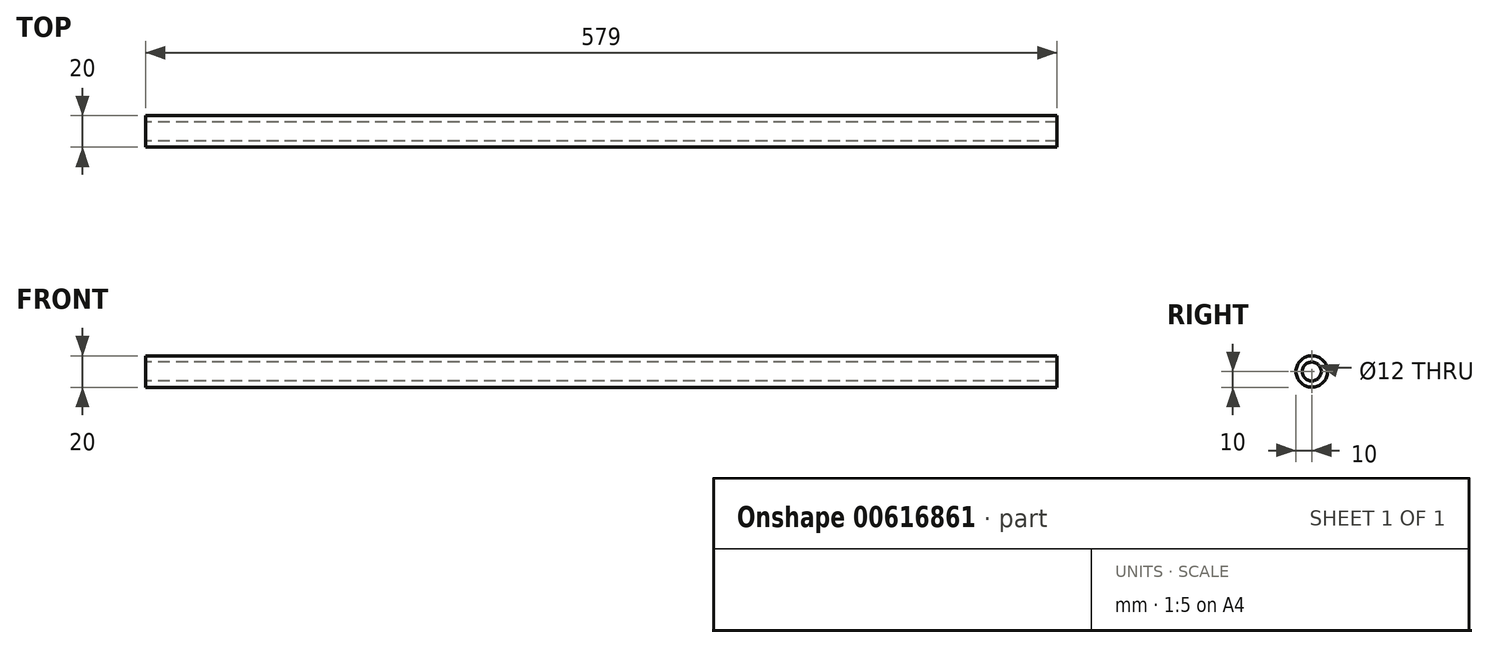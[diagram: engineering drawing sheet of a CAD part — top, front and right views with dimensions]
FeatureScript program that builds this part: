
annotation { "Feature Type Name" : "Feature", "Feature Type Description" : "" }
export const myFeature = defineFeature(function(context is Context, id is Id, definition is map)
    precondition{}
    {
        {
            var Q0;
            Q0=qCreatedBy(makeId("Right.planeOp"),FACE);
            var sketch = newSketch(context, id + "F0", { "sketchPlane" : qUnion([Q0])});
            skCircle(sketch, "E0", {"center": v(0, 0) * mm, "radius": 10 * mm});
            skCircle(sketch, "E1", {"center": v(0, 0) * mm, "radius": 6 * mm});
            skSolve(sketch);
        }
        {
            var Q0;
            Q0 = qSketchRegion(id + "F0", true);
            extrude(context, id + "F1", {"entities" : qUnion([Q0]), "depth" : 579 * mm, "offsetDistance" : 25 * mm, "symmetric" : true});
        }
    });
